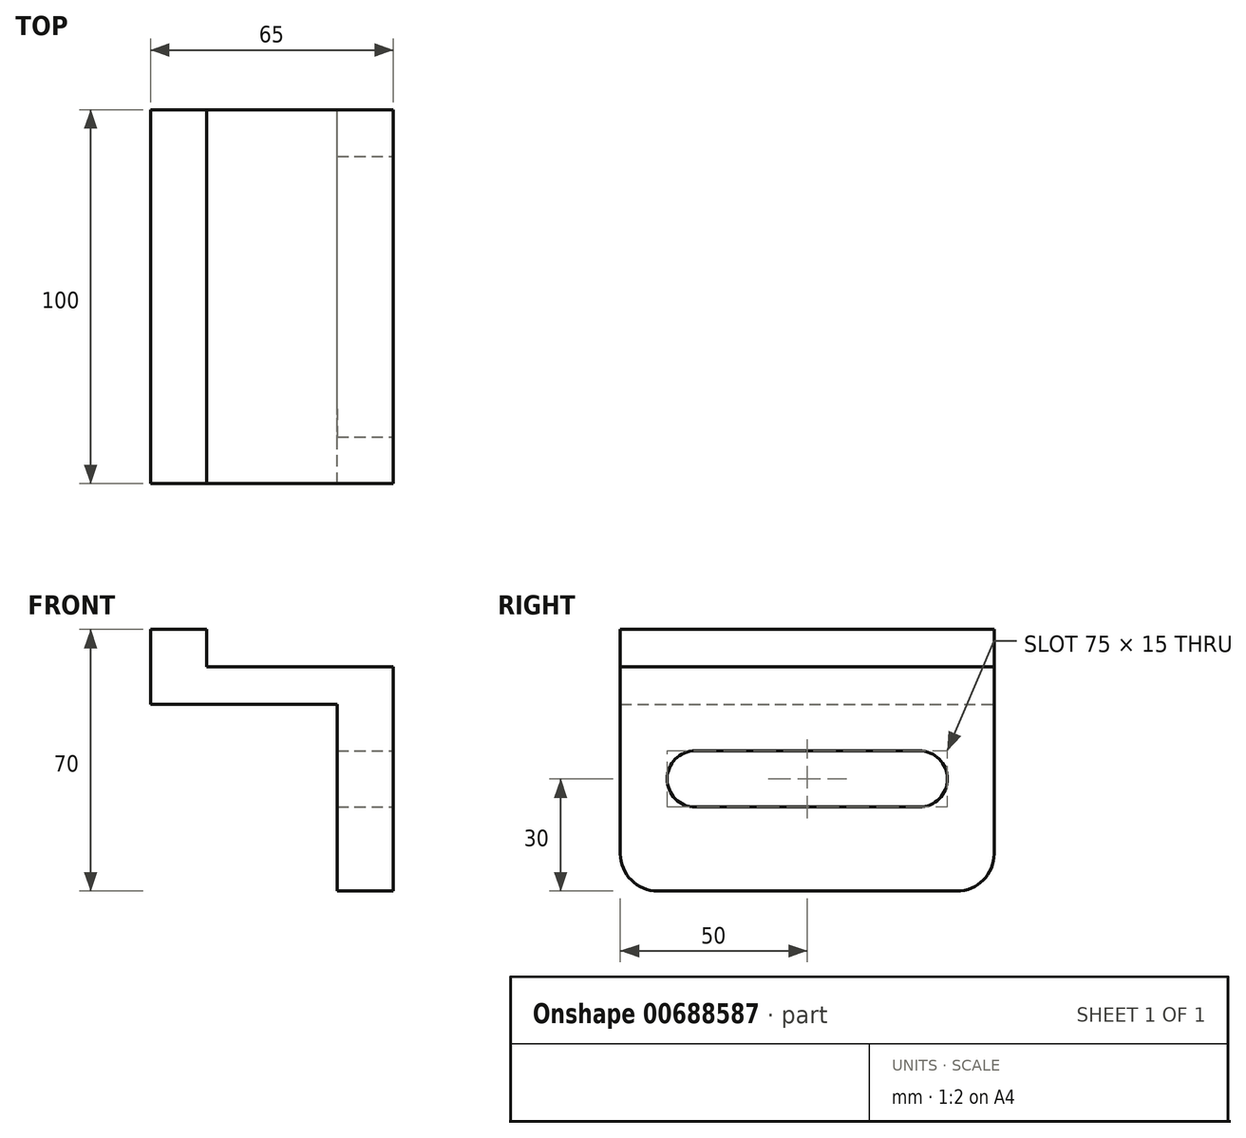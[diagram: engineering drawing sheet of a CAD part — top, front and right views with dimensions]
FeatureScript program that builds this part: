
annotation { "Feature Type Name" : "Feature", "Feature Type Description" : "" }
export const myFeature = defineFeature(function(context is Context, id is Id, definition is map)
    precondition{}
    {
        {
            var Q0;
            Q0=qCreatedBy(makeId("Front.planeOp"),FACE);
            var sketch = newSketch(context, id + "F0", { "sketchPlane" : qUnion([Q0])});
            skLineSegment(sketch, "E0", {"start": v(0, 0) * mm, "end": v(0, -20) * mm});
            skLineSegment(sketch, "E1", {"start": v(0, -20) * mm, "end": v(50, -20) * mm});
            skLineSegment(sketch, "E2", {"start": v(50, -20) * mm, "end": v(50, -70) * mm});
            skLineSegment(sketch, "E3", {"start": v(50, -70) * mm, "end": v(65, -70) * mm});
            skLineSegment(sketch, "E4", {"start": v(65, -70) * mm, "end": v(65, -10) * mm});
            skPoint(sketch, "E4.endSnap0", {"position": v(0, -10) * mm});
            skLineSegment(sketch, "E5", {"start": v(65, -10) * mm, "end": v(15, -10) * mm});
            skLineSegment(sketch, "E6", {"start": v(15, -10) * mm, "end": v(15, 0) * mm});
            skLineSegment(sketch, "E7", {"start": v(15, 0) * mm, "end": v(0, 0) * mm});
            skSolve(sketch);
        }
        {
            var Q0;
            Q0 = qSketchRegion(id + "F0", true);
            extrude(context, id + "F1", {"entities" : qUnion([Q0]), "depth" : 100 * mm, "offsetDistance" : 25 * mm});
        }
        {
            var Q0;
            Q0=makeQuery(id+"F1.opExtrude","SWEPT_FACE",FACE,{"disambiguationData":[OSD([sQuery(id+"F0.wireOp",EDGE,"E4")])]});
            var sketch = newSketch(context, id + "F2", { "sketchPlane" : qUnion([Q0])});
            skArc(sketch, "E8", {"start": v(-80, -32.5) * mm, "mid": v(-87.5, -40) * mm, "end": v(-80, -47.5) * mm});
            skPoint(sketch, "E8.centerSnap0", {"position": v(-100, -40) * mm});
            skArc(sketch, "E9", {"start": v(-20, -47.5) * mm, "mid": v(-12.5, -40) * mm, "end": v(-20, -32.5) * mm});
            skLineSegment(sketch, "E10", {"start": v(-80, -32.5) * mm, "end": v(-20, -32.5) * mm});
            skLineSegment(sketch, "E11", {"start": v(-80, -47.5) * mm, "end": v(-20, -47.5) * mm});
            skSolve(sketch);
        }
        {
            var Q0;
            Q0 = qSketchRegion(id + "F2", true);
            extrude(context, id + "F3", {"entities" : qUnion([Q0]), "operationType" : NewBodyOperationType.REMOVE, "oppositeDirection" : true, "depth" : 25 * mm, "offsetDistance" : 25 * mm});
        }
        {
            var Q0;
            Q0=makeQuery(id+"F1.opExtrude","CAP_EDGE",EDGE,{"disambiguationData":[OSD([sQuery(id+"F0.wireOp",EDGE,"E3")])],"isStart":false});
            var Q1;
            Q1=makeQuery(id+"F1.opExtrude","CAP_EDGE",EDGE,{"disambiguationData":[OSD([sQuery(id+"F0.wireOp",EDGE,"E3")])],"isStart":true});
            fillet(context, id + "F4", {"entities" : qUnion([Q0, Q1]), "radius" : 10 * mm, "tangentPropagation" : true, "allowEdgeOverflow" : false});
        }
    });
